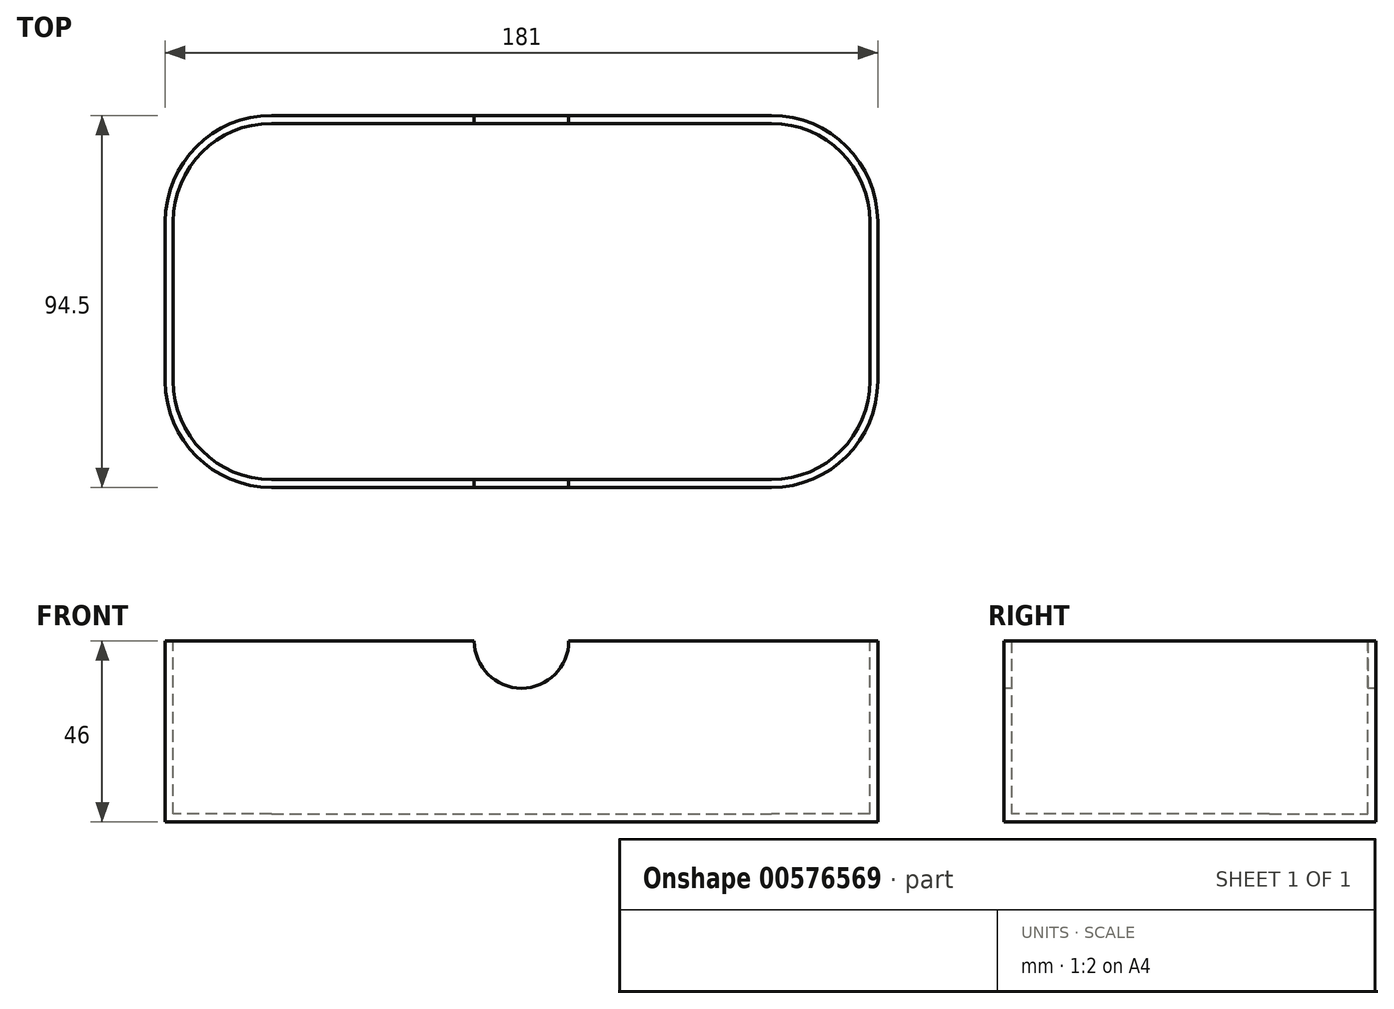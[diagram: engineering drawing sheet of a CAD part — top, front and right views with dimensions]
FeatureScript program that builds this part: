
annotation { "Feature Type Name" : "Feature", "Feature Type Description" : "" }
export const myFeature = defineFeature(function(context is Context, id is Id, definition is map)
    precondition{}
    {
        {
            var Q0;
            Q0=qCreatedBy(makeId("Top.planeOp"),FACE);
            var sketch = newSketch(context, id + "F0", { "sketchPlane" : qUnion([Q0])});
            skLineSegment(sketch, "E0.bottom", {"start": v(-100.24, 25.33) * mm, "end": v(80.76, 25.33) * mm});
            skLineSegment(sketch, "E0.top", {"start": v(-100.24, -69.17) * mm, "end": v(80.76, -69.17) * mm});
            skLineSegment(sketch, "E0.left", {"start": v(-100.24, 25.33) * mm, "end": v(-100.24, -69.17) * mm});
            skLineSegment(sketch, "E0.right", {"start": v(80.76, 25.33) * mm, "end": v(80.76, -69.17) * mm});
            skSolve(sketch);
        }
        {
            var Q0;
            Q0=makeQuery(id+"F0.imprint","IMPRINT",FACE,{"disambiguationData":[TD([[makeQuery(id+"F0.imprint","IMPRINT",EDGE,{"derivedFrom":sQuery(id+"F0.wireOp",EDGE,"E0.bottom")}),-1.0]])]});
            extrude(context, id + "F1", {"entities" : qUnion([Q0]), "oppositeDirection" : true, "depth" : 46 * mm, "offsetDistance" : 25 * mm});
        }
        {
            var Q0;
            Q0=makeQuery(id+"Fy4fcuLH8duHX1p_1.boolean.opBoolean","COPY",EDGE,{"derivedFrom":makeQuery(id+"Fy4fcuLH8duHX1p_1.opExtrude","SWEPT_EDGE",EDGE,{"disambiguationData":[OSD([sQuery(id+"FQ1VOp5YyVEmwT2_1.wireOp",EDGE,"AbOnBCwG-ejEu-1yyX-kLx1-Uw1KgbwVBsNr.bottom"),sQuery(id+"FQ1VOp5YyVEmwT2_1.wireOp",EDGE,"AbOnBCwG-ejEu-1yyX-kLx1-Uw1KgbwVBsNr.left")])]})});
            var Q1;
            Q1=makeQuery(id+"Fy4fcuLH8duHX1p_1.boolean.opBoolean","COPY",EDGE,{"derivedFrom":makeQuery(id+"Fy4fcuLH8duHX1p_1.opExtrude","SWEPT_EDGE",EDGE,{"disambiguationData":[OSD([sQuery(id+"FQ1VOp5YyVEmwT2_1.wireOp",EDGE,"AbOnBCwG-ejEu-1yyX-kLx1-Uw1KgbwVBsNr.top"),sQuery(id+"FQ1VOp5YyVEmwT2_1.wireOp",EDGE,"AbOnBCwG-ejEu-1yyX-kLx1-Uw1KgbwVBsNr.left")])]})});
            var Q2;
            Q2=makeQuery(id+"Fy4fcuLH8duHX1p_1.boolean.opBoolean","COPY",EDGE,{"derivedFrom":makeQuery(id+"Fy4fcuLH8duHX1p_1.opExtrude","SWEPT_EDGE",EDGE,{"disambiguationData":[OSD([sQuery(id+"FQ1VOp5YyVEmwT2_1.wireOp",EDGE,"AbOnBCwG-ejEu-1yyX-kLx1-Uw1KgbwVBsNr.top"),sQuery(id+"FQ1VOp5YyVEmwT2_1.wireOp",EDGE,"AbOnBCwG-ejEu-1yyX-kLx1-Uw1KgbwVBsNr.right")])]})});
            var Q3;
            Q3=makeQuery(id+"Fy4fcuLH8duHX1p_1.boolean.opBoolean","COPY",EDGE,{"derivedFrom":makeQuery(id+"Fy4fcuLH8duHX1p_1.opExtrude","SWEPT_EDGE",EDGE,{"disambiguationData":[OSD([sQuery(id+"FQ1VOp5YyVEmwT2_1.wireOp",EDGE,"AbOnBCwG-ejEu-1yyX-kLx1-Uw1KgbwVBsNr.bottom"),sQuery(id+"FQ1VOp5YyVEmwT2_1.wireOp",EDGE,"AbOnBCwG-ejEu-1yyX-kLx1-Uw1KgbwVBsNr.right")])]})});
            var Q4;
            Q4=makeQuery(id+"Fy4fcuLH8duHX1p_1.boolean.opBoolean","COPY",EDGE,{"derivedFrom":makeQuery(id+"Fy4fcuLH8duHX1p_1.opExtrude","SWEPT_EDGE",EDGE,{"disambiguationData":[OSD([sQuery(id+"FQ1VOp5YyVEmwT2_1.wireOp",EDGE,"0PEnAI3Q-vOqX-mtl6-auwA-NBIPJwzdRfqB.top"),sQuery(id+"FQ1VOp5YyVEmwT2_1.wireOp",EDGE,"0PEnAI3Q-vOqX-mtl6-auwA-NBIPJwzdRfqB.left")])]})});
            var Q5;
            Q5=makeQuery(id+"Fy4fcuLH8duHX1p_1.boolean.opBoolean","COPY",EDGE,{"derivedFrom":makeQuery(id+"Fy4fcuLH8duHX1p_1.opExtrude","SWEPT_EDGE",EDGE,{"disambiguationData":[OSD([sQuery(id+"FQ1VOp5YyVEmwT2_1.wireOp",EDGE,"0PEnAI3Q-vOqX-mtl6-auwA-NBIPJwzdRfqB.bottom"),sQuery(id+"FQ1VOp5YyVEmwT2_1.wireOp",EDGE,"0PEnAI3Q-vOqX-mtl6-auwA-NBIPJwzdRfqB.left")])]})});
            var Q6;
            Q6=makeQuery(id+"Fy4fcuLH8duHX1p_1.boolean.opBoolean","COPY",EDGE,{"derivedFrom":makeQuery(id+"Fy4fcuLH8duHX1p_1.opExtrude","SWEPT_EDGE",EDGE,{"disambiguationData":[OSD([sQuery(id+"FQ1VOp5YyVEmwT2_1.wireOp",EDGE,"0PEnAI3Q-vOqX-mtl6-auwA-NBIPJwzdRfqB.top"),sQuery(id+"FQ1VOp5YyVEmwT2_1.wireOp",EDGE,"0PEnAI3Q-vOqX-mtl6-auwA-NBIPJwzdRfqB.right")])]})});
            var Q7;
            Q7=makeQuery(id+"Fy4fcuLH8duHX1p_1.boolean.opBoolean","COPY",EDGE,{"derivedFrom":makeQuery(id+"Fy4fcuLH8duHX1p_1.opExtrude","SWEPT_EDGE",EDGE,{"disambiguationData":[OSD([sQuery(id+"FQ1VOp5YyVEmwT2_1.wireOp",EDGE,"0PEnAI3Q-vOqX-mtl6-auwA-NBIPJwzdRfqB.bottom"),sQuery(id+"FQ1VOp5YyVEmwT2_1.wireOp",EDGE,"0PEnAI3Q-vOqX-mtl6-auwA-NBIPJwzdRfqB.right")])]})});
            var Q8;
            Q8=makeQuery(id+"F1.opExtrude","SWEPT_EDGE",EDGE,{"disambiguationData":[OSD([sQuery(id+"F0.wireOp",EDGE,"E0.bottom"),sQuery(id+"F0.wireOp",EDGE,"E0.right")])]});
            var Q9;
            Q9=makeQuery(id+"F1.opExtrude","SWEPT_EDGE",EDGE,{"disambiguationData":[OSD([sQuery(id+"F0.wireOp",EDGE,"E0.bottom"),sQuery(id+"F0.wireOp",EDGE,"E0.left")])]});
            var Q10;
            Q10=makeQuery(id+"F1.opExtrude","SWEPT_EDGE",EDGE,{"disambiguationData":[OSD([sQuery(id+"F0.wireOp",EDGE,"E0.top"),sQuery(id+"F0.wireOp",EDGE,"E0.left")])]});
            var Q11;
            Q11=makeQuery(id+"F1.opExtrude","SWEPT_EDGE",EDGE,{"disambiguationData":[OSD([sQuery(id+"F0.wireOp",EDGE,"E0.top"),sQuery(id+"F0.wireOp",EDGE,"E0.right")])]});
            fillet(context, id + "F2", {"entities" : qUnion([Q0, Q1, Q2, Q3, Q4, Q5, Q6, Q7, Q8, Q9, Q10, Q11]), "radius" : 27 * mm, "tangentPropagation" : true, "allowEdgeOverflow" : false});
        }
        {
            var Q0;
            Q0=makeQuery(id+"F1.opExtrude","CAP_FACE",FACE,{"disambiguationData":[OSD([sQuery(id+"F0.wireOp",EDGE,"E0.bottom"),sQuery(id+"F0.wireOp",EDGE,"E0.top"),sQuery(id+"F0.wireOp",EDGE,"E0.left"),sQuery(id+"F0.wireOp",EDGE,"E0.right")])],"isStart":true});
            shell(context, id + "F3", {"entities" : qUnion([Q0]), "thickness" : 2 * mm});
        }
        {
            var Q0;
            Q0=makeQuery(id+"F1.opExtrude","SWEPT_FACE",FACE,{"disambiguationData":[OSD([sQuery(id+"F0.wireOp",EDGE,"E0.top")])]});
            var sketch = newSketch(context, id + "F4", { "sketchPlane" : qUnion([Q0])});
            skCircle(sketch, "E1", {"center": v(-9.74, 0) * mm, "radius": 12 * mm});
            skSolve(sketch);
        }
        {
            var Q0;
            Q0 = qSketchRegion(id + "F4", true);
            extrude(context, id + "F5", {"entities" : qUnion([Q0]), "operationType" : NewBodyOperationType.REMOVE, "oppositeDirection" : true, "depth" : 105 * mm, "offsetDistance" : 25 * mm});
        }
    });
